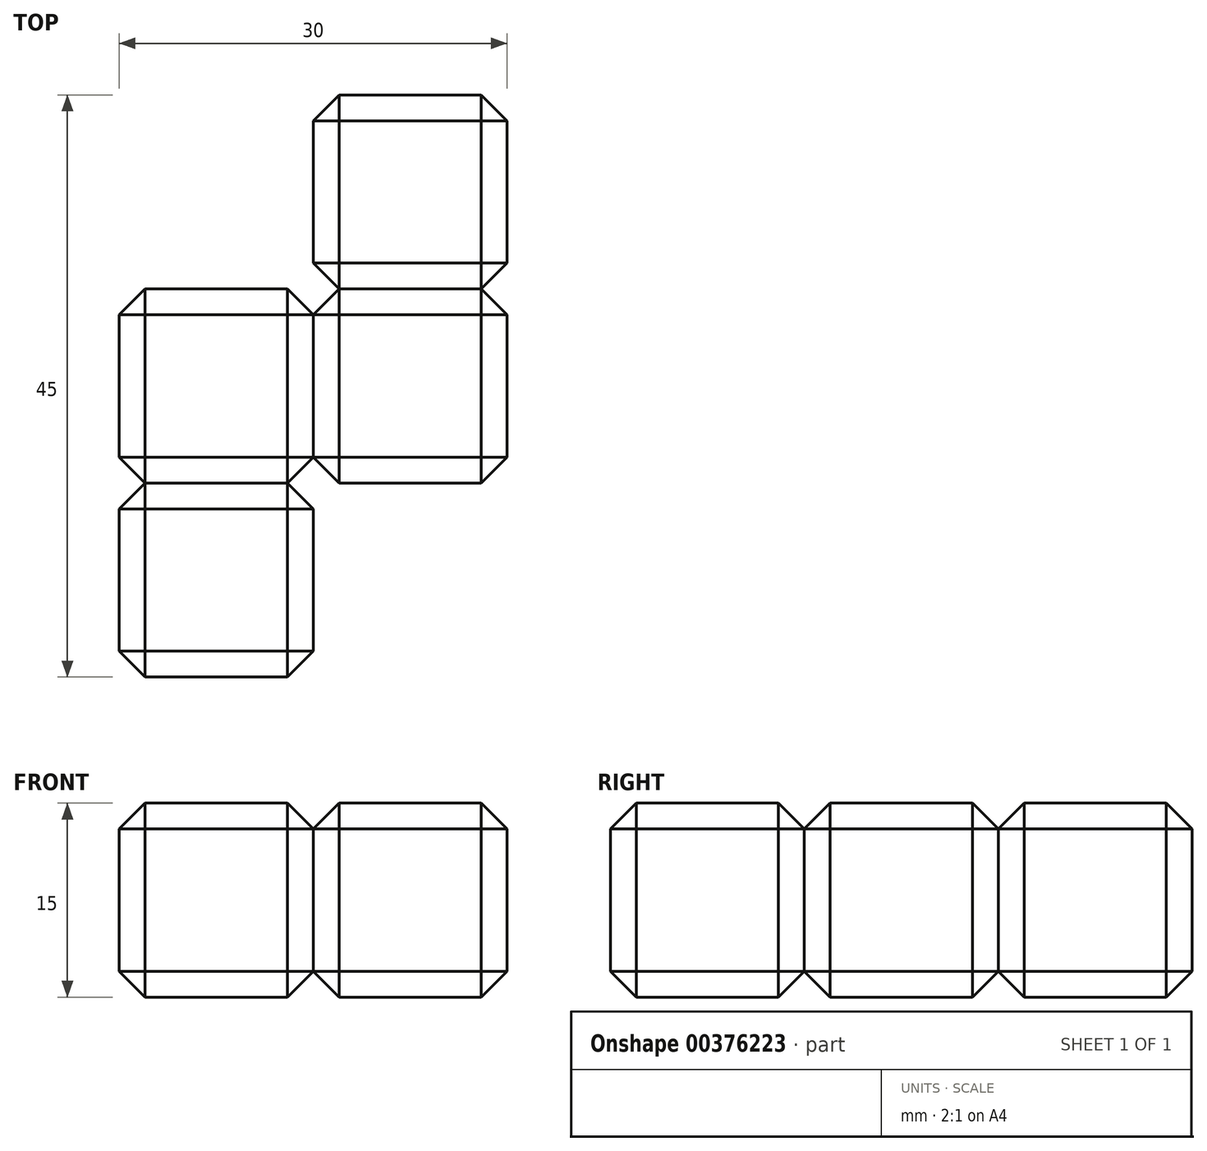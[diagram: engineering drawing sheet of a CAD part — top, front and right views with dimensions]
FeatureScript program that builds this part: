
annotation { "Feature Type Name" : "Feature", "Feature Type Description" : "" }
export const myFeature = defineFeature(function(context is Context, id is Id, definition is map)
    precondition{}
    {
        {
            var Q0;
            Q0=qCreatedBy(makeId("Front.planeOp"),FACE);
            var sketch = newSketch(context, id + "F0", { "sketchPlane" : qUnion([Q0])});
            skLineSegment(sketch, "E0.bottom", {"start": v(7.95, -7.5) * mm, "end": v(-7.05, -7.5) * mm});
            skLineSegment(sketch, "E0.top", {"start": v(7.95, 7.5) * mm, "end": v(-7.05, 7.5) * mm});
            skLineSegment(sketch, "E0.left", {"start": v(7.95, -7.5) * mm, "end": v(7.95, 7.5) * mm});
            skLineSegment(sketch, "E0.right", {"start": v(-7.05, -7.5) * mm, "end": v(-7.05, 7.5) * mm});
            skPoint(sketch, "E0.middle", {"position": v(0.45, 0) * mm});
            skSolve(sketch);
        }
        {
            var Q0;
            Q0 = qSketchRegion(id + "F0", true);
            extrude(context, id + "F1", {"entities" : qUnion([Q0]), "depth" : 15 * mm});
        }
        {
            var Q0;
            Q0=makeQuery(id+"F1.opExtrude","SWEPT_FACE",FACE,{"disambiguationData":[OSD([sQuery(id+"F0.wireOp",EDGE,"E0.top")])]});
            var Q1;
            Q1=makeQuery(id+"F1.opExtrude","CAP_FACE",FACE,{"disambiguationData":[OSD([sQuery(id+"F0.wireOp",EDGE,"E0.bottom"),sQuery(id+"F0.wireOp",EDGE,"E0.top"),sQuery(id+"F0.wireOp",EDGE,"E0.left"),sQuery(id+"F0.wireOp",EDGE,"E0.right")])],"isStart":false});
            var Q2;
            Q2=makeQuery(id+"F1.opExtrude","SWEPT_FACE",FACE,{"disambiguationData":[OSD([sQuery(id+"F0.wireOp",EDGE,"E0.left")])]});
            var Q3;
            Q3=makeQuery(id+"F1.opExtrude","CAP_FACE",FACE,{"disambiguationData":[OSD([sQuery(id+"F0.wireOp",EDGE,"E0.bottom"),sQuery(id+"F0.wireOp",EDGE,"E0.top"),sQuery(id+"F0.wireOp",EDGE,"E0.left"),sQuery(id+"F0.wireOp",EDGE,"E0.right")])],"isStart":true});
            var Q4;
            Q4=makeQuery(id+"F1.opExtrude","SWEPT_EDGE",EDGE,{"disambiguationData":[OSD([sQuery(id+"F0.wireOp",EDGE,"E0.bottom"),sQuery(id+"F0.wireOp",EDGE,"E0.right")])]});
            var Q5;
            Q5=makeQuery(id+"F1.opExtrude","SWEPT_FACE",FACE,{"disambiguationData":[OSD([sQuery(id+"F0.wireOp",EDGE,"E0.right")])]});
            chamfer(context, id + "F2", {"entities" : qUnion([Q0, Q1, Q2, Q3, Q4, Q5]), "width" : 2 * mm, "tangentPropagation" : true});
        }
        {
            var Q0;
            Q0=makeQuery(id+"F1.opExtrude","SWEPT_BODY",BODY,{"disambiguationData":[OSD([sQuery(id+"F0.wireOp",EDGE,"E0.bottom"),sQuery(id+"F0.wireOp",EDGE,"E0.top"),sQuery(id+"F0.wireOp",EDGE,"E0.left"),sQuery(id+"F0.wireOp",EDGE,"E0.right")])]});
            transform(context, id + "F3", {"entities" : qUnion([Q0]), "transformType" : TransformType.TRANSLATION_3D, "dx" : 15 * mm, "dy" : 0 * mm, "dz" : 0 * mm, "makeCopy" : true});
        }
        {
            var Q0;
            Q0=makeQuery(id+"F1.opExtrude","SWEPT_BODY",BODY,{"disambiguationData":[OSD([sQuery(id+"F0.wireOp",EDGE,"E0.bottom"),sQuery(id+"F0.wireOp",EDGE,"E0.top"),sQuery(id+"F0.wireOp",EDGE,"E0.left"),sQuery(id+"F0.wireOp",EDGE,"E0.right")])]});
            transform(context, id + "F4", {"entities" : qUnion([Q0]), "transformType" : TransformType.TRANSLATION_3D, "dx" : 0 * mm, "dy" : 15 * mm, "dz" : 0 * mm, "makeCopy" : true});
        }
        {
            var Q0;
            Q0=makeQuery(id+"F4.opPattern","COPY",BODY,{"derivedFrom":makeQuery(id+"F1.opExtrude","SWEPT_BODY",BODY,{"disambiguationData":[OSD([sQuery(id+"F0.wireOp",EDGE,"E0.bottom"),sQuery(id+"F0.wireOp",EDGE,"E0.top"),sQuery(id+"F0.wireOp",EDGE,"E0.left"),sQuery(id+"F0.wireOp",EDGE,"E0.right")])]}),"instanceName":"1"});
            transform(context, id + "F5", {"entities" : qUnion([Q0]), "transformType" : TransformType.TRANSLATION_3D, "dx" : 0 * mm, "dy" : 15 * mm, "dz" : 0 * mm, "makeCopy" : true});
        }
        {
            var Q0;
            Q0=makeQuery(id+"F5.opPattern","COPY",BODY,{"derivedFrom":makeQuery(id+"F4.opPattern","COPY",BODY,{"derivedFrom":makeQuery(id+"F1.opExtrude","SWEPT_BODY",BODY,{"disambiguationData":[OSD([sQuery(id+"F0.wireOp",EDGE,"E0.bottom"),sQuery(id+"F0.wireOp",EDGE,"E0.top"),sQuery(id+"F0.wireOp",EDGE,"E0.left"),sQuery(id+"F0.wireOp",EDGE,"E0.right")])]}),"instanceName":"1"}),"instanceName":"1"});
            deleteBodies(context, id + "F6", {"entities" : qUnion([Q0])});
        }
        {
            var Q0;
            Q0=makeQuery(id+"F3.opPattern","COPY",BODY,{"derivedFrom":makeQuery(id+"F1.opExtrude","SWEPT_BODY",BODY,{"disambiguationData":[OSD([sQuery(id+"F0.wireOp",EDGE,"E0.bottom"),sQuery(id+"F0.wireOp",EDGE,"E0.top"),sQuery(id+"F0.wireOp",EDGE,"E0.left"),sQuery(id+"F0.wireOp",EDGE,"E0.right")])]}),"instanceName":"1"});
            deleteBodies(context, id + "F7", {"entities" : qUnion([Q0])});
        }
        {
            var Q0;
            Q0=makeQuery(id+"F4.opPattern","COPY",BODY,{"derivedFrom":makeQuery(id+"F1.opExtrude","SWEPT_BODY",BODY,{"disambiguationData":[OSD([sQuery(id+"F0.wireOp",EDGE,"E0.bottom"),sQuery(id+"F0.wireOp",EDGE,"E0.top"),sQuery(id+"F0.wireOp",EDGE,"E0.left"),sQuery(id+"F0.wireOp",EDGE,"E0.right")])]}),"instanceName":"1"});
            transform(context, id + "F8", {"entities" : qUnion([Q0]), "transformType" : TransformType.TRANSLATION_3D, "dx" : 15 * mm, "dy" : 0 * mm, "dz" : 0 * mm, "makeCopy" : true});
        }
        {
            var Q0;
            Q0=makeQuery(id+"F8.opPattern","COPY",BODY,{"derivedFrom":makeQuery(id+"F4.opPattern","COPY",BODY,{"derivedFrom":makeQuery(id+"F1.opExtrude","SWEPT_BODY",BODY,{"disambiguationData":[OSD([sQuery(id+"F0.wireOp",EDGE,"E0.bottom"),sQuery(id+"F0.wireOp",EDGE,"E0.top"),sQuery(id+"F0.wireOp",EDGE,"E0.left"),sQuery(id+"F0.wireOp",EDGE,"E0.right")])]}),"instanceName":"1"}),"instanceName":"1"});
            transform(context, id + "F9", {"entities" : qUnion([Q0]), "transformType" : TransformType.TRANSLATION_3D, "dx" : 0 * mm, "dy" : 15 * mm, "dz" : 0 * mm, "makeCopy" : true});
        }
    });
